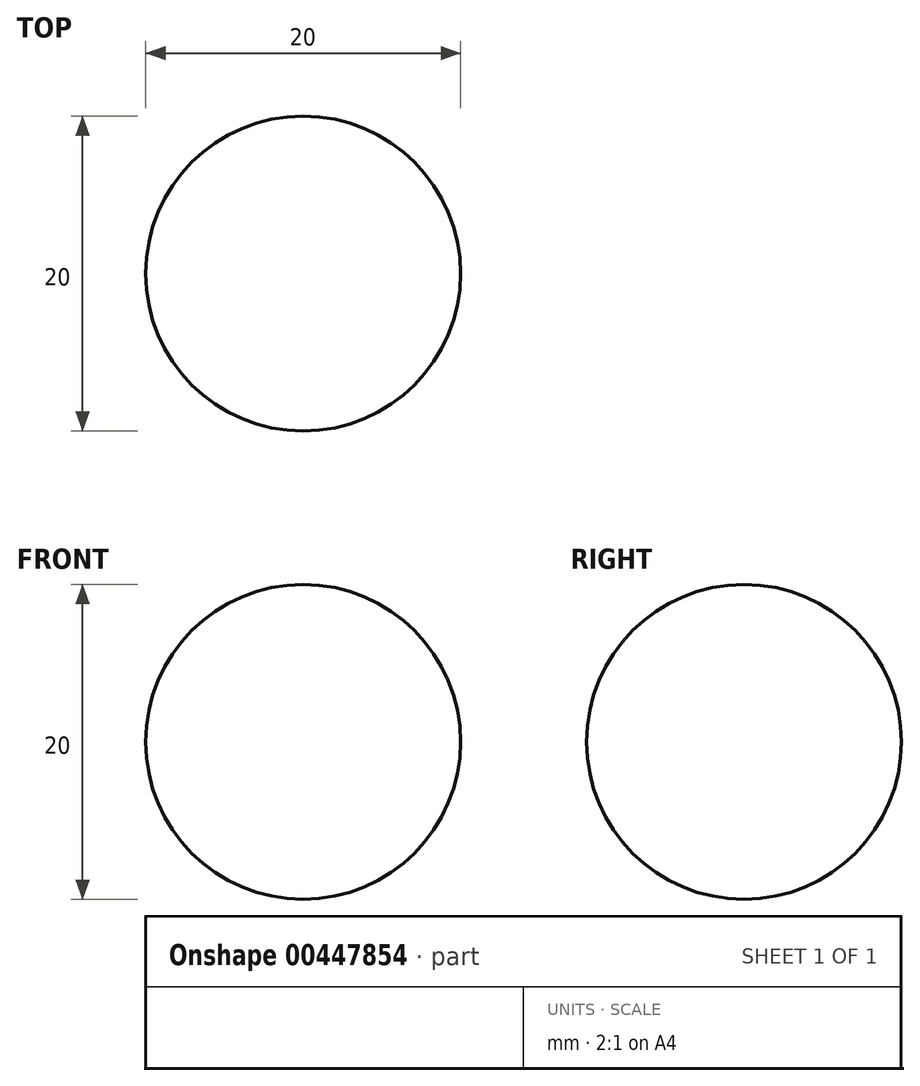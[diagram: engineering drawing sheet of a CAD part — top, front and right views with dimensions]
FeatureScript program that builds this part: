
annotation { "Feature Type Name" : "Feature", "Feature Type Description" : "" }
export const myFeature = defineFeature(function(context is Context, id is Id, definition is map)
    precondition{}
    {
        {
            var Q0;
            Q0=qCreatedBy(makeId("Front.planeOp"),FACE);
            var sketch = newSketch(context, id + "F0", { "sketchPlane" : qUnion([Q0])});
            skArc(sketch, "E0", {"start": v(0, -6.4) * mm, "mid": v(10, 3.6) * mm, "end": v(0, 13.6) * mm});
            skLineSegment(sketch, "E1", {"start": v(0, 13.6) * mm, "end": v(0, -6.4) * mm});
            skSolve(sketch);
        }
        {
            var Q0;
            Q0=makeQuery(id+"F0.imprint","IMPRINT",FACE,{"disambiguationData":[TD([[makeQuery(id+"F0.imprint","IMPRINT",EDGE,{"derivedFrom":sQuery(id+"F0.wireOp",EDGE,"E0")}),1.0]])]});
            var Q1;
            Q1=sQuery(id+"F0.wireOp",EDGE,"E1");
            revolve(context, id + "F1", {"entities" : qUnion([Q0]), "axis" : qUnion([Q1]), "revolveType" : RevolveType.FULL});
        }
    });
